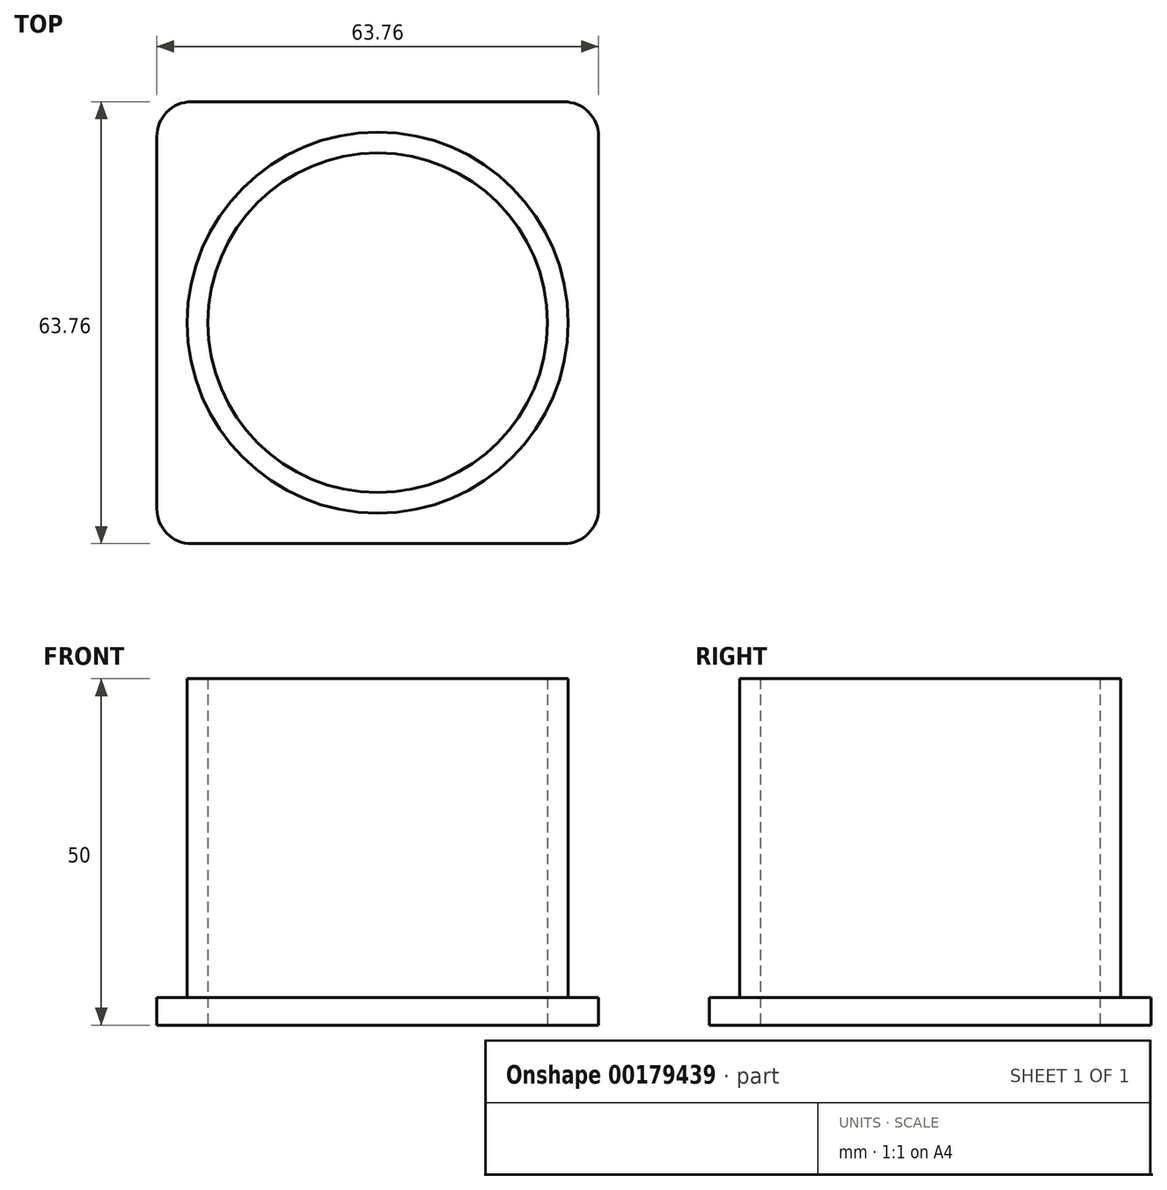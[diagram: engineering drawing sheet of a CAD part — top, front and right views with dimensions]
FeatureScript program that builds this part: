
annotation { "Feature Type Name" : "Feature", "Feature Type Description" : "" }
export const myFeature = defineFeature(function(context is Context, id is Id, definition is map)
    precondition{}
    {
        {
            var Q0;
            Q0=qCreatedBy(makeId("Top.planeOp"),FACE);
            var sketch = newSketch(context, id + "F0", { "sketchPlane" : qUnion([Q0])});
            skCircle(sketch, "E0", {"center": v(0, 0) * mm, "radius": 27.5 * mm});
            skCircle(sketch, "E1", {"center": v(0, 0) * mm, "radius": 24.5 * mm});
            skLineSegment(sketch, "E2.bottom", {"start": v(31.88, -31.88) * mm, "end": v(-31.88, -31.88) * mm});
            skLineSegment(sketch, "E2.top", {"start": v(31.88, 31.88) * mm, "end": v(-31.88, 31.88) * mm});
            skLineSegment(sketch, "E2.left", {"start": v(31.88, -31.88) * mm, "end": v(31.88, 31.88) * mm});
            skLineSegment(sketch, "E2.right", {"start": v(-31.88, -31.88) * mm, "end": v(-31.88, 31.88) * mm});
            skSolve(sketch);
        }
        {
            var Q0;
            Q0=makeQuery(id+"F0.imprint","IMPRINT",FACE,{"disambiguationData":[TD([[makeQuery(id+"F0.imprint","IMPRINT",EDGE,{"derivedFrom":sQuery(id+"F0.wireOp",EDGE,"E0")}),-1.0]])]});
            extrude(context, id + "F1", {"entities" : qUnion([Q0]), "depth" : 4 * mm});
        }
        {
            var Q0;
            Q0=makeQuery(id+"F0.imprint","IMPRINT",FACE,{"disambiguationData":[TD([[makeQuery(id+"F0.imprint","IMPRINT",EDGE,{"derivedFrom":sQuery(id+"F0.wireOp",EDGE,"E0")}),1.0]])]});
            extrude(context, id + "F2", {"entities" : qUnion([Q0]), "operationType" : NewBodyOperationType.ADD, "depth" : 50 * mm});
        }
        {
            var Q0;
            Q0=makeQuery(id+"F1.opExtrude","SWEPT_EDGE",EDGE,{"disambiguationData":[OSD([sQuery(id+"F0.wireOp",EDGE,"E2.bottom"),sQuery(id+"F0.wireOp",EDGE,"E2.right")])]});
            var Q1;
            Q1=makeQuery(id+"F1.opExtrude","SWEPT_EDGE",EDGE,{"disambiguationData":[OSD([sQuery(id+"F0.wireOp",EDGE,"E2.bottom"),sQuery(id+"F0.wireOp",EDGE,"E2.left")])]});
            var Q2;
            Q2=makeQuery(id+"F1.opExtrude","SWEPT_EDGE",EDGE,{"disambiguationData":[OSD([sQuery(id+"F0.wireOp",EDGE,"E2.top"),sQuery(id+"F0.wireOp",EDGE,"E2.left")])]});
            var Q3;
            Q3=makeQuery(id+"F1.opExtrude","SWEPT_EDGE",EDGE,{"disambiguationData":[OSD([sQuery(id+"F0.wireOp",EDGE,"E2.top"),sQuery(id+"F0.wireOp",EDGE,"E2.right")])]});
            fillet(context, id + "F3", {"entities" : qUnion([Q0, Q1, Q2, Q3]), "radius" : 5 * mm, "tangentPropagation" : true, "allowEdgeOverflow" : false});
        }
    });
